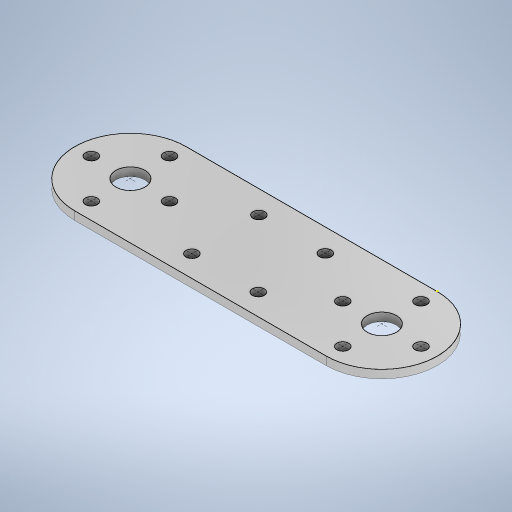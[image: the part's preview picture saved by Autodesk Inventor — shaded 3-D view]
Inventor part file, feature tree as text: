
AUTODESK INVENTOR PART (.ipt)
format: ipt  version: 2024.2 (Build 282272000, 272)  size: 263,680 bytes
history: native  units: in
note: dims shown in document units (in); Inventor stores cm internally (conversion verified against a paired STEP export)
features: sketch x1, extrude x1
ambient origin geometry x8: Origin, YZ Plane, XZ Plane, XY Plane, X Axis, Y Axis, Z Axis, Center Point
bodies: Solid1 (feature_tree)
feature tree (2):
  sketch  "Sketch1"  dims[d0=0.0591in d1=0.0in]
  extrude  "Extrusion1"  [1 undecoded]
note: 1 required parameter value undecoded (feature->parameter linkage not recoverable at this tier; creation-order binding heuristic only, values carry confidence <= 0.55)
